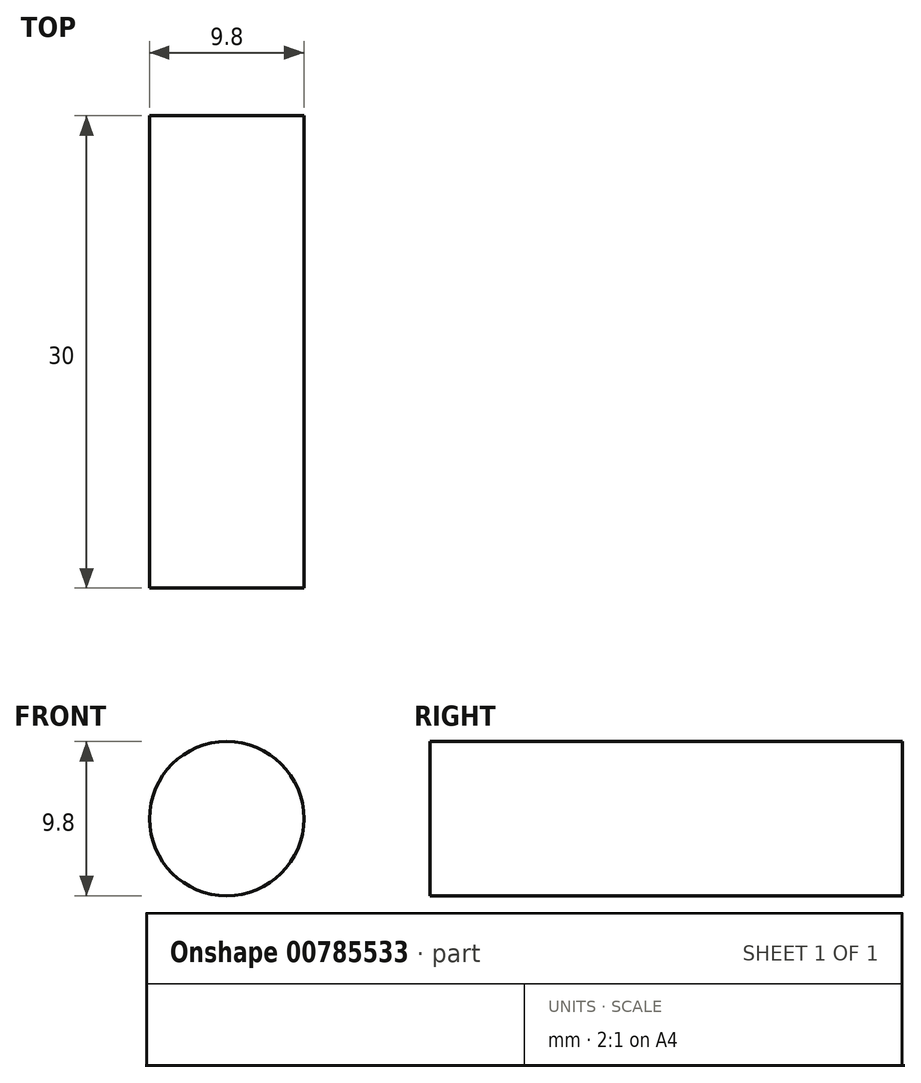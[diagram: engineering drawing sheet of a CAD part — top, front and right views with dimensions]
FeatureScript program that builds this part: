
annotation { "Feature Type Name" : "Feature", "Feature Type Description" : "" }
export const myFeature = defineFeature(function(context is Context, id is Id, definition is map)
    precondition{}
    {
        {
            var Q0;
            Q0=qCreatedBy(makeId("Front.planeOp"),FACE);
            var sketch = newSketch(context, id + "F0", { "sketchPlane" : qUnion([Q0])});
            skCircle(sketch, "E0", {"center": v(0, 0) * mm, "radius": 4.9 * mm});
            skSolve(sketch);
        }
        {
            var Q0;
            Q0 = qSketchRegion(id + "F0", true);
            extrude(context, id + "F1", {"entities" : qUnion([Q0]), "depth" : 30 * mm, "offsetDistance" : 25 * mm});
        }
    });
